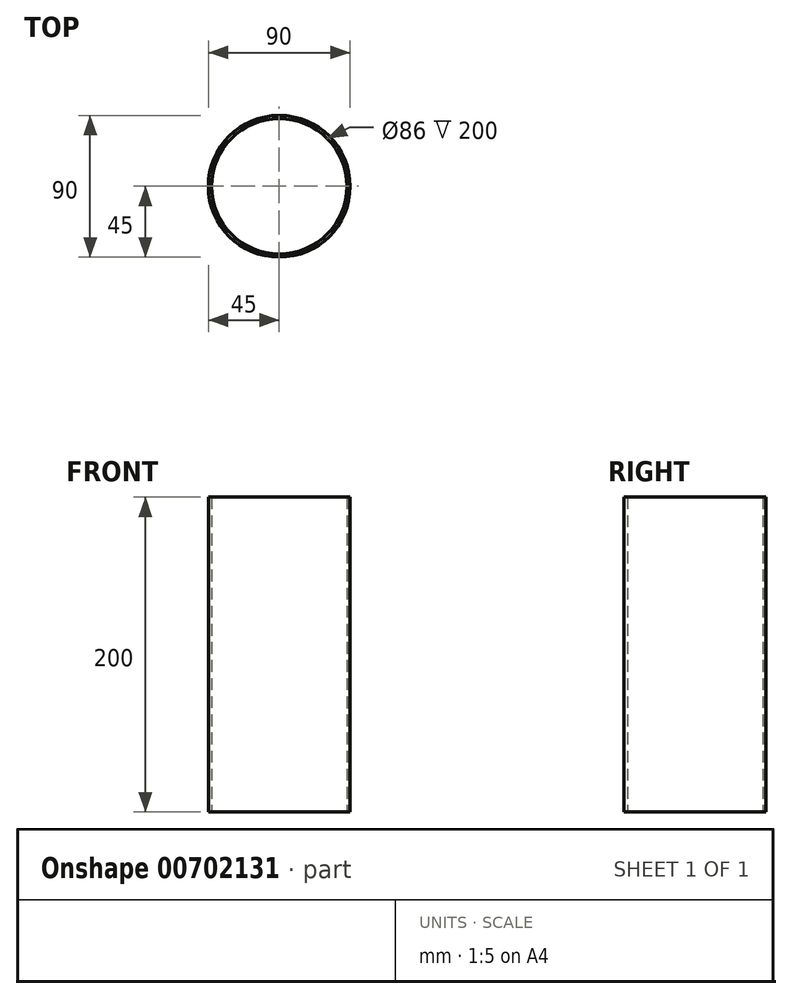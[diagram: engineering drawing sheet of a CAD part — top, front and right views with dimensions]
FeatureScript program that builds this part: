
annotation { "Feature Type Name" : "Feature", "Feature Type Description" : "" }
export const myFeature = defineFeature(function(context is Context, id is Id, definition is map)
    precondition{}
    {
        {
            var Q0;
            Q0=qCreatedBy(makeId("Top.planeOp"),FACE);
            var sketch = newSketch(context, id + "F0", { "sketchPlane" : qUnion([Q0])});
            skCircle(sketch, "E0", {"center": v(0, 0) * mm, "radius": 45 * mm});
            skCircle(sketch, "E1", {"center": v(0, 0) * mm, "radius": 43 * mm});
            skSolve(sketch);
        }
        {
            var Q0;
            Q0=makeQuery(id+"F0.imprint","IMPRINT",FACE,{"disambiguationData":[TD([[makeQuery(id+"F0.imprint","IMPRINT",EDGE,{"derivedFrom":sQuery(id+"F0.wireOp",EDGE,"E0")}),1.0]])]});
            extrude(context, id + "F1", {"entities" : qUnion([Q0]), "depth" : 200 * mm, "offsetDistance" : 25 * mm});
        }
    });
